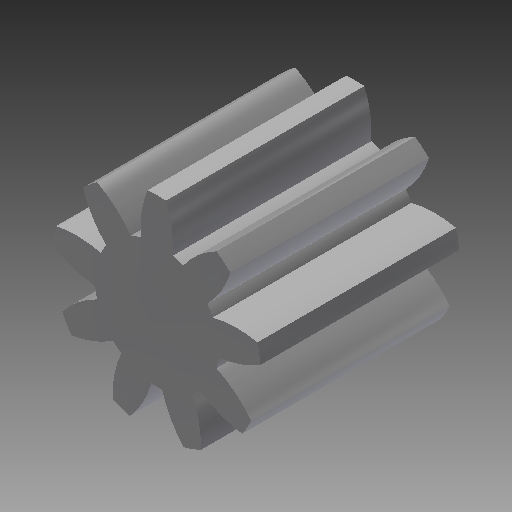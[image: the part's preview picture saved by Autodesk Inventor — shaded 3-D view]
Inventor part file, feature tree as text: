
AUTODESK INVENTOR PART (.ipt)
format: ipt  version: 2019 (Build 230136000, 136)  size: 195,584 bytes
history: native  units: mm (DEFAULTED — no unit token found)
features: plane x3, other x3, sketch x2, extrude x1
ambient origin geometry x8: Origin, YZ Plane, XZ Plane, XY Plane, X Axis, Y Axis, Z Axis, Center Point
bodies: Solid1 (feature_tree)
feature tree (9):
  extrude  "Extrusion1"  Depth=2.3mm TaperAngle=0.0deg
  plane  "Work Plane2"
  plane  "Work Plane8"
  plane  "Work Plane9"
  other  "Spur Gear"
  sketch  "Sketch1"  dims[d0=2.415579mm d1=2.3mm d2=0.0mm]
  sketch  "Sketch2"  dims[d3=2.0mm d4=10.0mm d5=0.0mm d16=6.0mm d17=0.0mm d34=3.490659mm d39=0.0mm d41=0.0mm d43=6.0mm d46=6.0mm d47=0.0mm d48=0.0mm]
  other  "Srf1"
  other  "Pitch Diameter"
